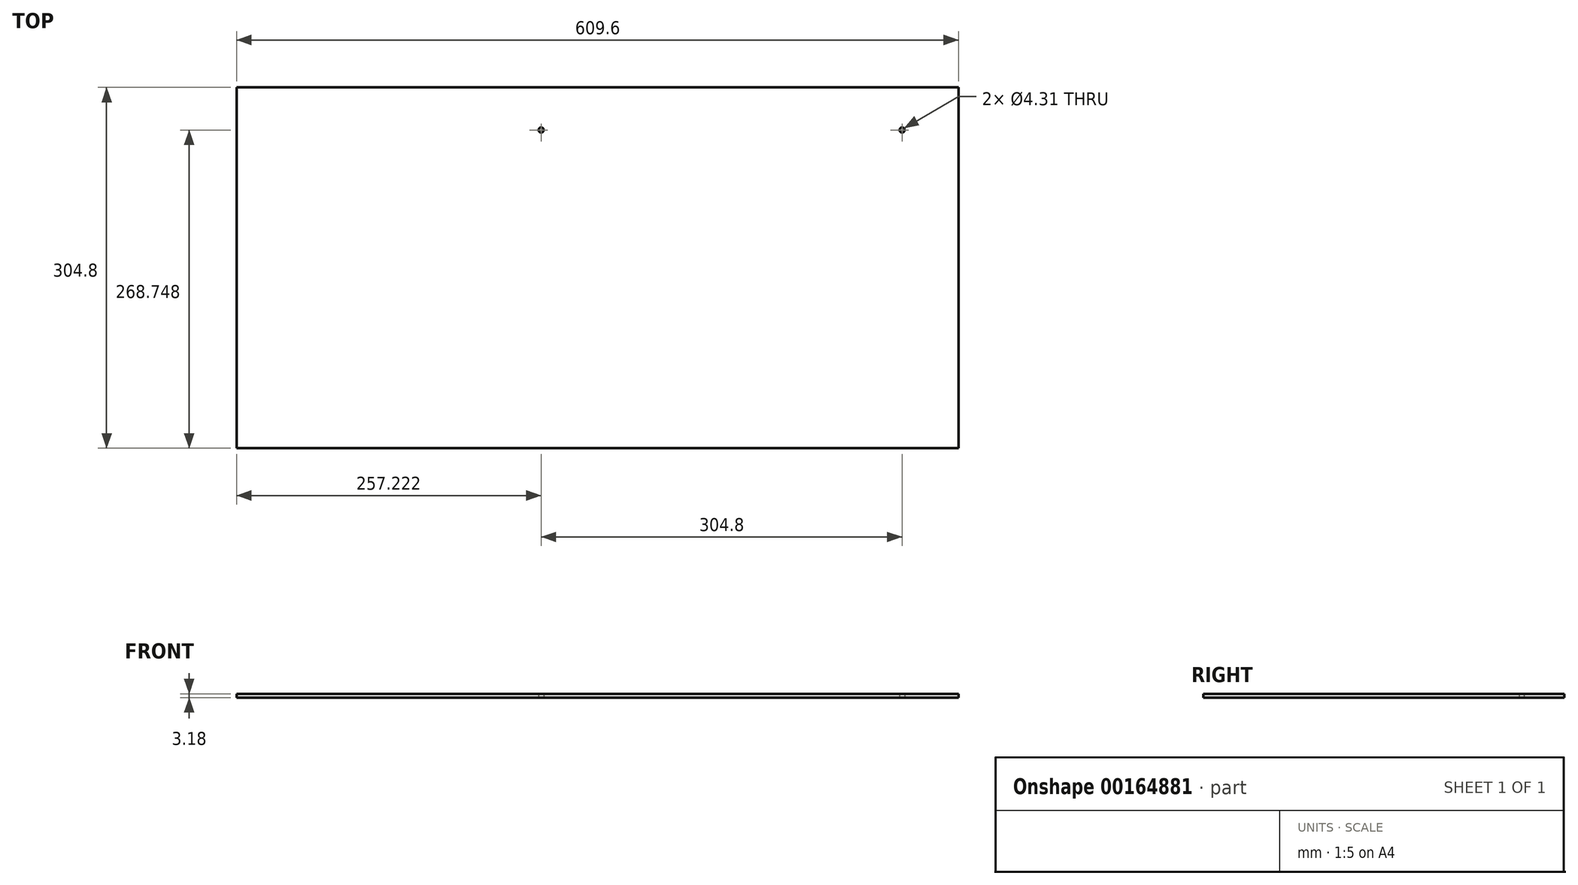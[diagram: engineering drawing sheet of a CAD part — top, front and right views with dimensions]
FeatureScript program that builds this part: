
annotation { "Feature Type Name" : "Feature", "Feature Type Description" : "" }
export const myFeature = defineFeature(function(context is Context, id is Id, definition is map)
    precondition{}
    {
        {
            var Q0;
            Q0=qCreatedBy(makeId("Top.planeOp"),FACE);
            var sketch = newSketch(context, id + "F0", { "sketchPlane" : qUnion([Q0])});
            skLineSegment(sketch, "E0.bottom", {"start": v(0, 0) * mm, "end": v(609.6, 0) * mm});
            skLineSegment(sketch, "E0.top", {"start": v(0, 304.8) * mm, "end": v(609.6, 304.8) * mm});
            skLineSegment(sketch, "E0.left", {"start": v(0, 0) * mm, "end": v(0, 304.8) * mm});
            skLineSegment(sketch, "E0.right", {"start": v(609.6, 0) * mm, "end": v(609.6, 304.8) * mm});
            skLineSegment(sketch, "E1", {"start": v(609.6, 268.75) * mm, "end": v(562.02, 268.75) * mm, "construction": true});
            skLineSegment(sketch, "E2", {"start": v(562.02, 268.75) * mm, "end": v(562.02, 304.8) * mm, "construction": true});
            skCircle(sketch, "E3", {"center": v(562.02, 268.75) * mm, "radius": 2.15 * mm});
            skCircle(sketch, "E4", {"center": v(257.22, 268.75) * mm, "radius": 2.15 * mm});
            skLineSegment(sketch, "E5", {"start": v(257.22, 268.75) * mm, "end": v(562.02, 268.75) * mm, "construction": true});
            skSolve(sketch);
        }
        {
            var Q0;
            Q0 = qSketchRegion(id + "F0", true);
            extrude(context, id + "F1", {"entities" : qUnion([Q0]), "depth" : 3.17 * mm});
        }
    });
